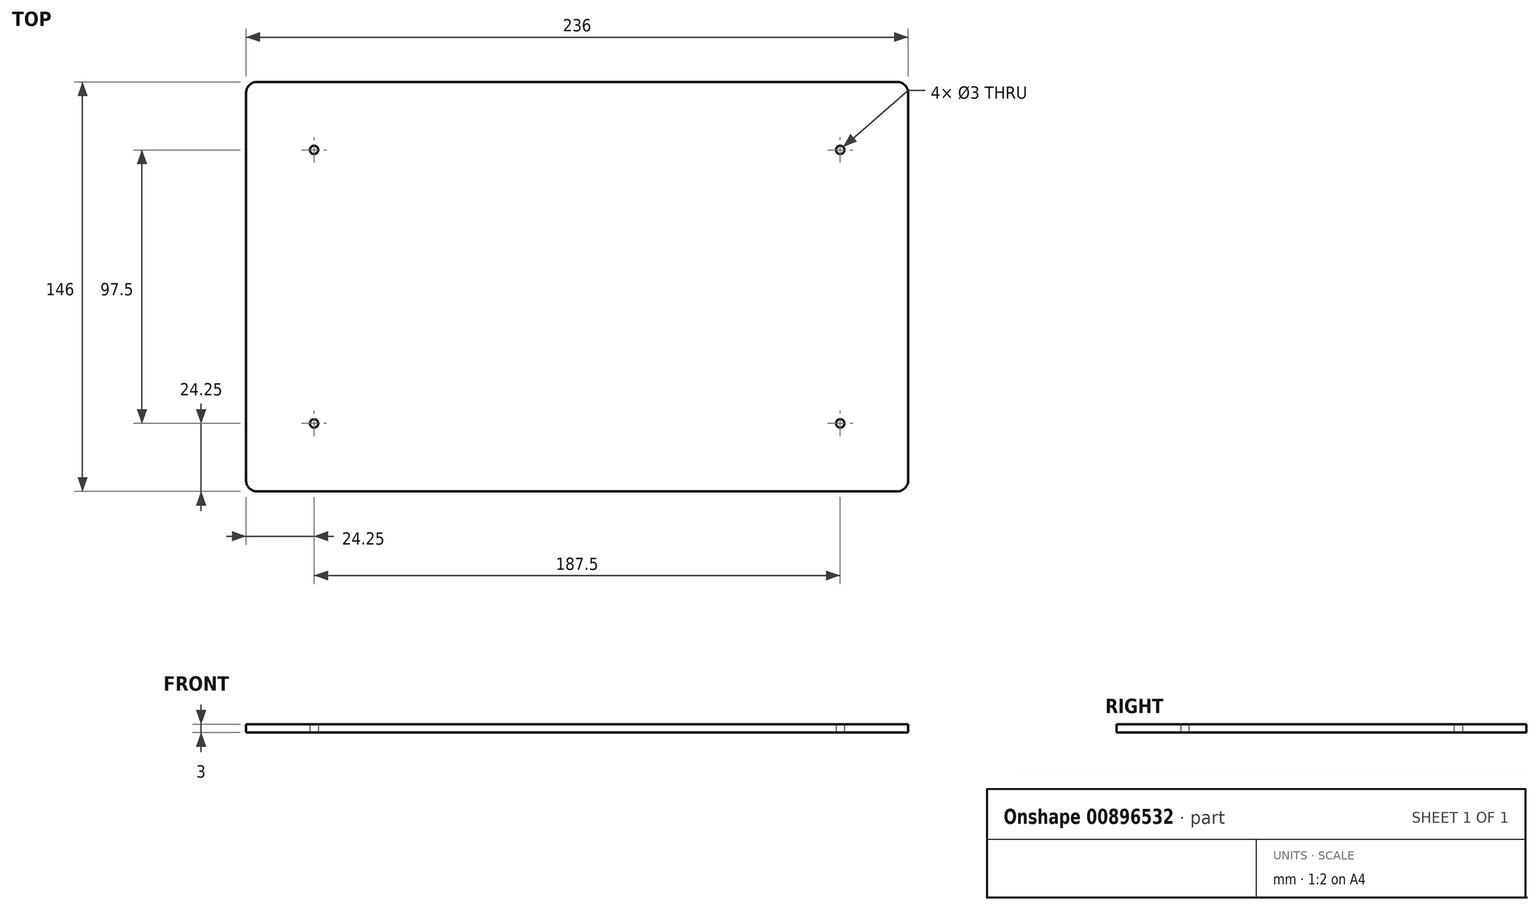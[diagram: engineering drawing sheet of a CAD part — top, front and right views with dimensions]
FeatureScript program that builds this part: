
annotation { "Feature Type Name" : "Feature", "Feature Type Description" : "" }
export const myFeature = defineFeature(function(context is Context, id is Id, definition is map)
    precondition{}
    {
        {
            assignVariable(context, id + "F0", {"variableType" : VariableType.LENGTH, "name" : "thickness", "lengthValue" : 3 * mm});
        }
        {
            var Q0;
            Q0=qCreatedBy(makeId("Top.planeOp"),FACE);
            var sketch = newSketch(context, id + "F1", { "sketchPlane" : qUnion([Q0])});
            skLineSegment(sketch, "E0.bottom", {"start": v(0, 0) * mm, "end": v(236, 0) * mm});
            skLineSegment(sketch, "E0.top", {"start": v(0, 146) * mm, "end": v(236, 146) * mm});
            skLineSegment(sketch, "E0.left", {"start": v(0, 0) * mm, "end": v(0, 146) * mm});
            skLineSegment(sketch, "E0.right", {"start": v(236, 0) * mm, "end": v(236, 146) * mm});
            skLineSegment(sketch, "E1.bottom", {"start": v(24.25, 24.25) * mm, "end": v(211.75, 24.25) * mm, "construction": true});
            skLineSegment(sketch, "E1.top", {"start": v(24.25, 121.75) * mm, "end": v(211.75, 121.75) * mm, "construction": true});
            skLineSegment(sketch, "E1.left", {"start": v(24.25, 24.25) * mm, "end": v(24.25, 121.75) * mm, "construction": true});
            skLineSegment(sketch, "E1.right", {"start": v(211.75, 24.25) * mm, "end": v(211.75, 121.75) * mm, "construction": true});
            skLineSegment(sketch, "E2", {"start": v(118, 146) * mm, "end": v(118, 121.75) * mm, "construction": true});
            skLineSegment(sketch, "E3", {"start": v(211.75, 73) * mm, "end": v(236, 73) * mm, "construction": true});
            skCircle(sketch, "E4", {"center": v(24.25, 121.75) * mm, "radius": 1.5 * mm});
            skCircle(sketch, "E5", {"center": v(211.75, 121.75) * mm, "radius": 1.5 * mm});
            skCircle(sketch, "E6", {"center": v(211.75, 24.25) * mm, "radius": 1.5 * mm});
            skCircle(sketch, "E7", {"center": v(24.25, 24.25) * mm, "radius": 1.5 * mm});
            skSolve(sketch);
        }
        {
            var Q0;
            Q0 = qSketchRegion(id + "F1", true);
            extrude(context, id + "F2", {"entities" : qUnion([Q0]), "depth" : getVariable(context, 'thickness'), "offsetDistance" : 25 * mm});
        }
        {
            var Q0;
            Q0=makeQuery(id+"F2.opExtrude","SWEPT_EDGE",EDGE,{"disambiguationData":[OSD([sQuery(id+"F1.wireOp",EDGE,"E0.bottom"),sQuery(id+"F1.wireOp",EDGE,"E0.left")])]});
            var Q1;
            Q1=makeQuery(id+"F2.opExtrude","SWEPT_EDGE",EDGE,{"disambiguationData":[OSD([sQuery(id+"F1.wireOp",EDGE,"E0.top"),sQuery(id+"F1.wireOp",EDGE,"E0.left")])]});
            var Q2;
            Q2=makeQuery(id+"F2.opExtrude","SWEPT_EDGE",EDGE,{"disambiguationData":[OSD([sQuery(id+"F1.wireOp",EDGE,"E0.top"),sQuery(id+"F1.wireOp",EDGE,"E0.right")])]});
            var Q3;
            Q3=makeQuery(id+"F2.opExtrude","SWEPT_EDGE",EDGE,{"disambiguationData":[OSD([sQuery(id+"F1.wireOp",EDGE,"E0.bottom"),sQuery(id+"F1.wireOp",EDGE,"E0.right")])]});
            fillet(context, id + "F3", {"entities" : qUnion([Q0, Q1, Q2, Q3]), "radius" : 4 * mm, "tangentPropagation" : true, "allowEdgeOverflow" : false});
        }
    });
